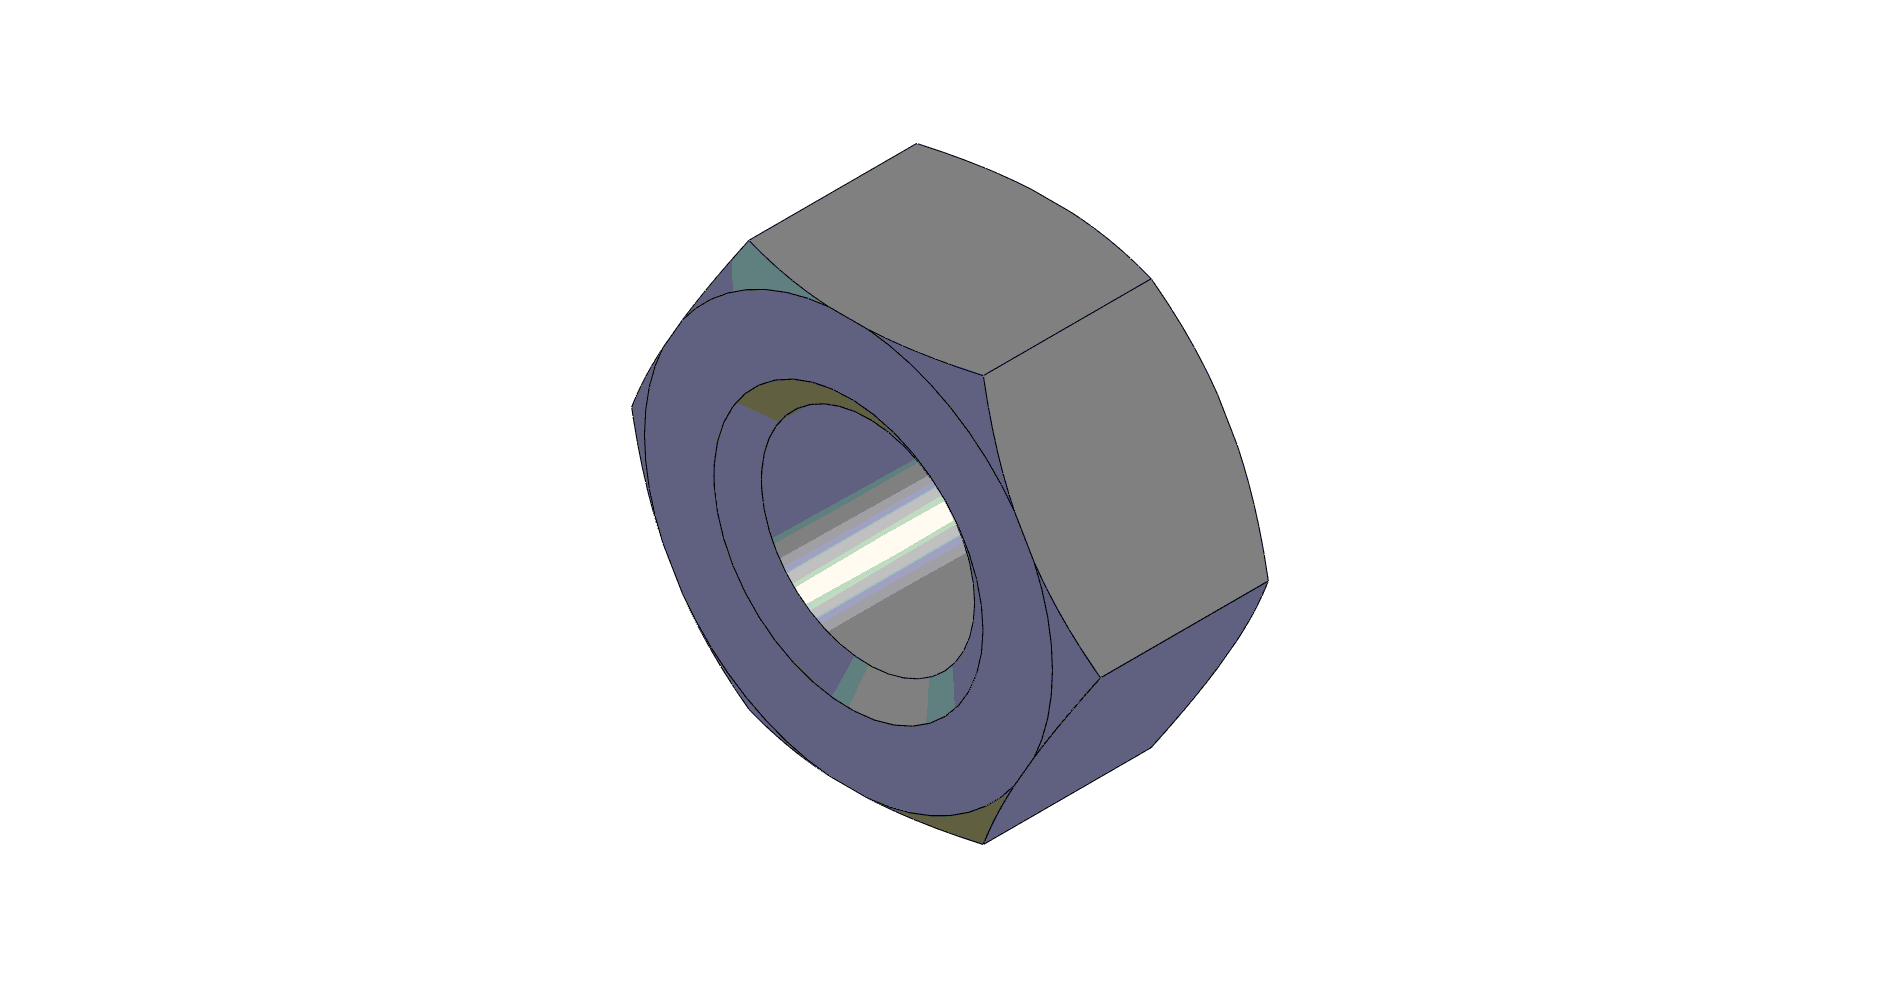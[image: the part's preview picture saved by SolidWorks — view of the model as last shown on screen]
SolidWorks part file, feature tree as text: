
SOLIDWORKS PART (.sldprt)
format: sldprt  version: not decoded by parser v0  size: 195,584 bytes
history: native  units: mm
features: sketch x4, plane x3, material x1, extrude x1, cut_revolve x1, hole x1, thread x1 (+13 scaffold rows collapsed)
feature tree (25):
  scaffold x13  (default folders/planes/origin — collapsed)
  material  "Материал <не указан>"
  plane  "Спереди"
  plane  "Сверху"
  plane  "Справа"
  sketch  "Эскиз1"  dims[D1=8.0mm]
  extrude  "Бобышка-Вытянуть1"  Depth=4mm
  sketch  "Эскиз2"  dims[c1.D1=~2.309401mm c2.D1=30.0deg c2.D2=0.6mm]
  cut_revolve  "Вырез-Повернуть2"  Angle=360deg
  hole  "Отверстие обработанное метчиком M51"  [1 undecoded]
  sketch  "Эскиз4"
  sketch  "Эскиз3"  dims[hole-wizard template sketch: 46 standard entries collapsed; hole parameters kept: c15.Диаметр проходного сверла=4.2mm c15.Глубина проходного сверла=4.0mm c15.Диаметр передней зенковки=5.3mm c15.D4=~3.666174mm c15.Угол передней зенковки=110.0deg c15.Диаметр задней зенковки=5.3mm c15.D6=~9.919017mm c15.Угол задней зенковки=110.0deg]
  thread  "Отверстие резьбы1"  Diameter=5mm  [1 undecoded]
decode coverage: 6 of 8 modeling features carry decoded parameters
note: ~ marks probable driven/reference dimensions
note: 2 parameter values undecoded
note: suppression state not decoded; provenance and decode notes live in map.json
